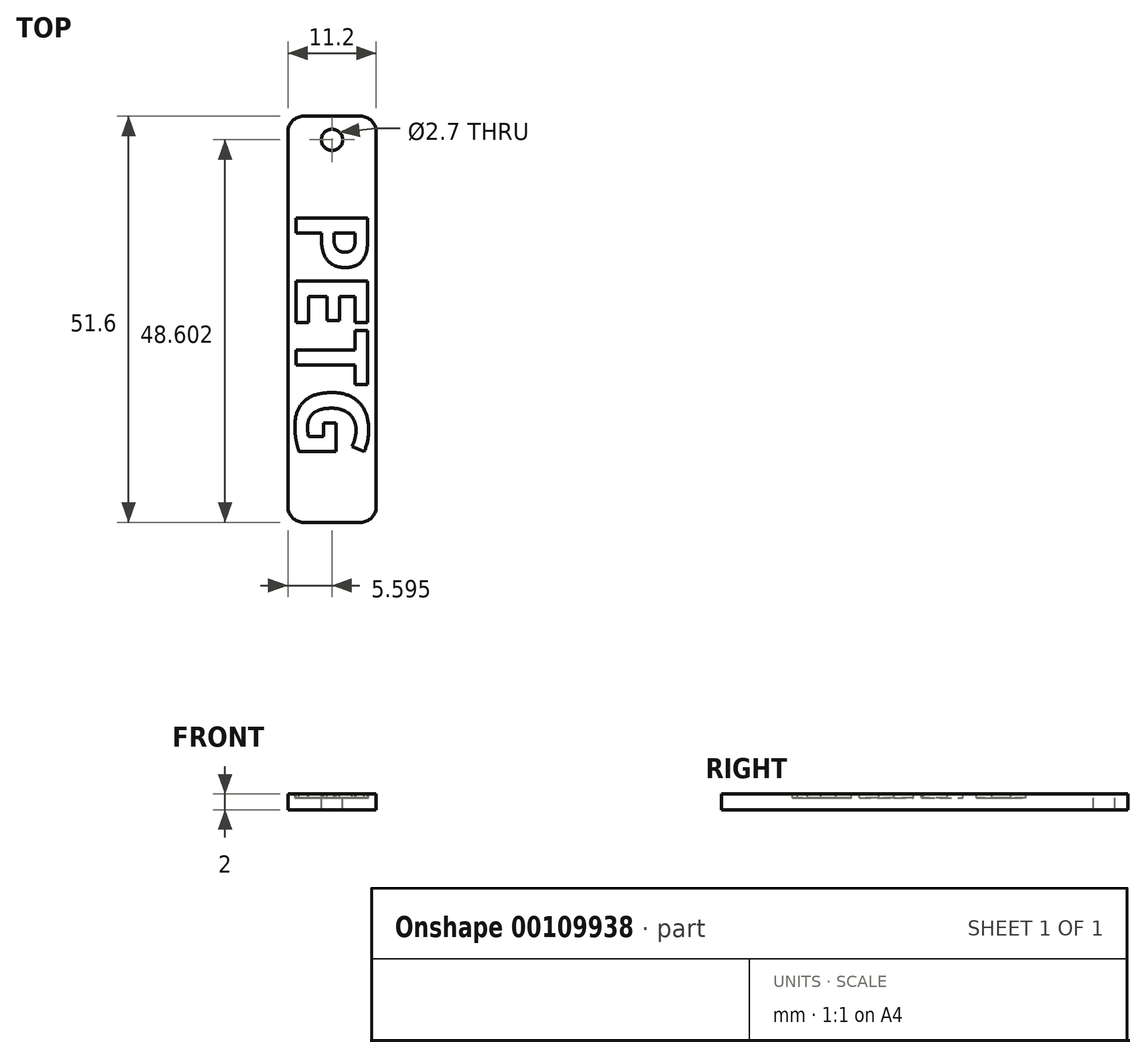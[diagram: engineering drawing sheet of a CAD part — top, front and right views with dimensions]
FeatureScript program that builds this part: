
annotation { "Feature Type Name" : "Feature", "Feature Type Description" : "" }
export const myFeature = defineFeature(function(context is Context, id is Id, definition is map)
    precondition{}
    {
        {
            var Q0;
            Q0=qCreatedBy(makeId("Top.planeOp"),FACE);
            var sketch = newSketch(context, id + "F0", { "sketchPlane" : qUnion([Q0])});
            skLineSegment(sketch, "E0.bottom", {"start": v(-49.26, 76.92) * mm, "end": v(-38.06, 76.92) * mm});
            skLineSegment(sketch, "E0.top", {"start": v(-49.26, 25.32) * mm, "end": v(-38.06, 25.32) * mm});
            skLineSegment(sketch, "E0.left", {"start": v(-49.26, 76.92) * mm, "end": v(-49.26, 25.32) * mm});
            skLineSegment(sketch, "E0.right", {"start": v(-38.06, 76.92) * mm, "end": v(-38.06, 25.32) * mm});
            skCircle(sketch, "E1", {"center": v(-43.66, 73.92) * mm, "radius": 1.35 * mm});
            skText(sketch, "E2", { "text": "PETG", "fontName": "OpenSans-Bold.ttf"});
            const initialGuessF0  = {"E2": [-0.04826, 0.06514, 0, -1, 0.0092]};
            skSetInitialGuess(sketch, initialGuessF0);
            skSolve(sketch);
        }
        {
            var Q0;
            Q0=makeQuery(id+"F0.imprint","IMPRINT",FACE,{"disambiguationData":[TD([[makeQuery(id+"F0.imprint","IMPRINT",EDGE,{"derivedFrom":sQuery(id+"F0.wireOp",EDGE,"E0.bottom")}),-1.0]])]});
            var Q1;
            Q1=makeQuery(id+"F0.imprint","IMPRINT",FACE,{"disambiguationData":[TD([[makeQuery(id+"F0.imprint","IMPRINT",EDGE,{"derivedFrom":sQuery(id+"F0.wireOp",EDGE,"E2.sketch_text.stroke-0")}),-1.0]])]});
            var Q2;
            Q2=makeQuery(id+"F0.imprint","IMPRINT",FACE,{"disambiguationData":[TD([[makeQuery(id+"F0.imprint","IMPRINT",EDGE,{"derivedFrom":sQuery(id+"F0.wireOp",EDGE,"E2.sketch_text.stroke-0")}),1.0]])]});
            var Q3;
            Q3=makeQuery(id+"F0.imprint","IMPRINT",FACE,{"disambiguationData":[TD([[makeQuery(id+"F0.imprint","IMPRINT",EDGE,{"derivedFrom":sQuery(id+"F0.wireOp",EDGE,"E2.sketch_text.stroke-16")}),-1.0]])]});
            var Q4;
            Q4=makeQuery(id+"F0.imprint","IMPRINT",FACE,{"disambiguationData":[TD([[makeQuery(id+"F0.imprint","IMPRINT",EDGE,{"derivedFrom":sQuery(id+"F0.wireOp",EDGE,"E2.sketch_text.stroke-28")}),-1.0]])]});
            var Q5;
            Q5=makeQuery(id+"F0.imprint","IMPRINT",FACE,{"disambiguationData":[TD([[makeQuery(id+"F0.imprint","IMPRINT",EDGE,{"derivedFrom":sQuery(id+"F0.wireOp",EDGE,"E2.sketch_text.stroke-36")}),-1.0]])]});
            extrude(context, id + "F1", {"entities" : qUnion([Q0, Q1, Q2, Q3, Q4, Q5]), "oppositeDirection" : true, "depth" : 2 * mm});
        }
        {
            var Q0;
            Q0=makeQuery(id+"F0.imprint","IMPRINT",FACE,{"disambiguationData":[TD([[makeQuery(id+"F0.imprint","IMPRINT",EDGE,{"derivedFrom":sQuery(id+"F0.wireOp",EDGE,"E2.sketch_text.stroke-0")}),-1.0]])]});
            var Q1;
            Q1=makeQuery(id+"F0.imprint","IMPRINT",FACE,{"disambiguationData":[TD([[makeQuery(id+"F0.imprint","IMPRINT",EDGE,{"derivedFrom":sQuery(id+"F0.wireOp",EDGE,"E2.sketch_text.stroke-16")}),-1.0]])]});
            var Q2;
            Q2=makeQuery(id+"F0.imprint","IMPRINT",FACE,{"disambiguationData":[TD([[makeQuery(id+"F0.imprint","IMPRINT",EDGE,{"derivedFrom":sQuery(id+"F0.wireOp",EDGE,"E2.sketch_text.stroke-28")}),-1.0]])]});
            var Q3;
            Q3=makeQuery(id+"F0.imprint","IMPRINT",FACE,{"disambiguationData":[TD([[makeQuery(id+"F0.imprint","IMPRINT",EDGE,{"derivedFrom":sQuery(id+"F0.wireOp",EDGE,"E2.sketch_text.stroke-36")}),-1.0]])]});
            var Q4;
            Q4=qConstructionFilter(qBodyType(qCreatedBy(id+"F0",EDGE),BodyType.WIRE),ConstructionObject.NO);
            extrude(context, id + "F2", {"entities" : qUnion([Q0, Q1, Q2, Q3]), "operationType" : NewBodyOperationType.REMOVE, "surfaceEntities" : qUnion([Q4]), "oppositeDirection" : true, "depth" : .5 * mm});
        }
        {
            var Q0;
            Q0=makeQuery(id+"F1.opExtrude","SWEPT_EDGE",EDGE,{"disambiguationData":[OSD([sQuery(id+"F0.wireOp",EDGE,"E0.bottom"),sQuery(id+"F0.wireOp",EDGE,"E0.left")])]});
            var Q1;
            Q1=makeQuery(id+"F1.opExtrude","SWEPT_EDGE",EDGE,{"disambiguationData":[OSD([sQuery(id+"F0.wireOp",EDGE,"E0.bottom"),sQuery(id+"F0.wireOp",EDGE,"E0.right")])]});
            var Q2;
            Q2=makeQuery(id+"F1.opExtrude","SWEPT_EDGE",EDGE,{"disambiguationData":[OSD([sQuery(id+"F0.wireOp",EDGE,"E0.top"),sQuery(id+"F0.wireOp",EDGE,"E0.right")])]});
            var Q3;
            Q3=makeQuery(id+"F1.opExtrude","SWEPT_EDGE",EDGE,{"disambiguationData":[OSD([sQuery(id+"F0.wireOp",EDGE,"E0.top"),sQuery(id+"F0.wireOp",EDGE,"E0.left")])]});
            fillet(context, id + "F3", {"entities" : qUnion([Q0, Q1, Q2, Q3]), "radius" : 2 * mm, "tangentPropagation" : true, "allowEdgeOverflow" : false});
        }
    });
